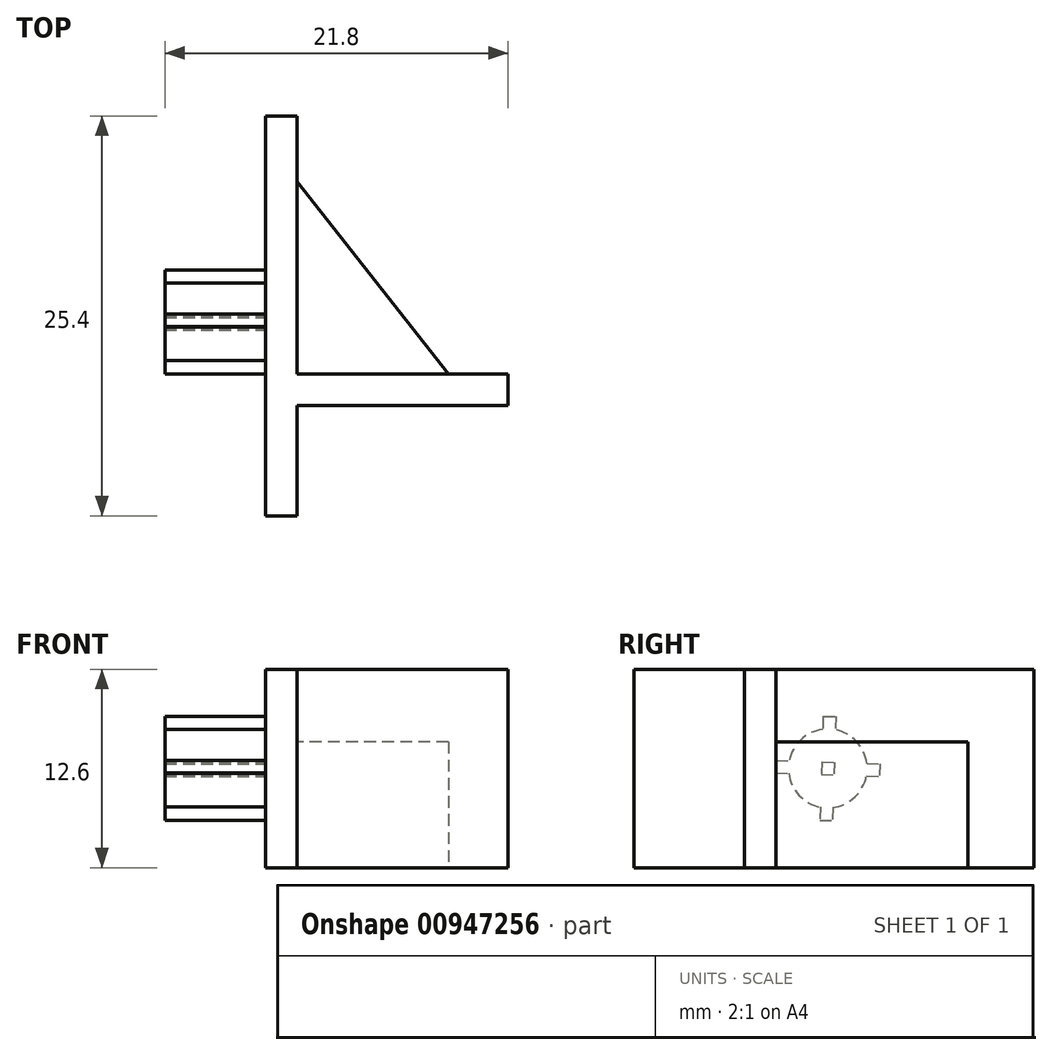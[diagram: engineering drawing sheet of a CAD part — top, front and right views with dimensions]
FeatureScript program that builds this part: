
annotation { "Feature Type Name" : "Feature", "Feature Type Description" : "" }
export const myFeature = defineFeature(function(context is Context, id is Id, definition is map)
    precondition{}
    {
        {
            var Q0;
            Q0=qCreatedBy(makeId("Top.planeOp"),FACE);
            var sketch = newSketch(context, id + "F0", { "sketchPlane" : qUnion([Q0])});
            skLineSegment(sketch, "E0", {"start": v(0, -10.12) * mm, "end": v(0, 15.28) * mm});
            skLineSegment(sketch, "E1", {"start": v(0, -10.12) * mm, "end": v(2, -10.12) * mm});
            skLineSegment(sketch, "E2", {"start": v(2, -10.12) * mm, "end": v(2, -3.12) * mm});
            skLineSegment(sketch, "E3", {"start": v(2, -3.12) * mm, "end": v(15.4, -3.12) * mm});
            skLineSegment(sketch, "E4", {"start": v(15.4, -3.12) * mm, "end": v(15.4, -1.12) * mm});
            skLineSegment(sketch, "E5", {"start": v(15.4, -1.12) * mm, "end": v(2, -1.12) * mm});
            skLineSegment(sketch, "E6", {"start": v(2, -1.12) * mm, "end": v(2, 15.28) * mm});
            skLineSegment(sketch, "E7", {"start": v(2, 15.28) * mm, "end": v(0, 15.28) * mm});
            skLineSegment(sketch, "E8", {"start": v(11.6, -1.12) * mm, "end": v(2, 11.1) * mm});
            skSolve(sketch);
        }
        {
            var Q0;
            {var subQ3=sQuery(id+"F0.wireOp",EDGE,"E8");Q0=makeQuery(id+"F0.imprint","IMPRINT",FACE,{"disambiguationData":[TD([[makeQuery(id+"F0.imprint","IMPRINT",EDGE,{"derivedFrom":subQ3}),1.0]])]});}
            extrude(context, id + "F1", {"entities" : qUnion([Q0]), "depth" : 8 * mm, "offsetDistance" : 25 * mm});
        }
        {
            var Q0;
            Q0=makeQuery(id+"F0.imprint","IMPRINT",FACE,{"disambiguationData":[TD([[makeQuery(id+"F0.imprint","IMPRINT",EDGE,{"derivedFrom":sQuery(id+"F0.wireOp",EDGE,"E0")}),-1.0]])]});
            extrude(context, id + "F2", {"entities" : qUnion([Q0]), "operationType" : NewBodyOperationType.ADD, "depth" : 12.6 * mm, "offsetDistance" : 25 * mm});
        }
        {
            var Q0;
            Q0=makeQuery(id+"F2.opExtrude","SWEPT_FACE",FACE,{"disambiguationData":[OSD([sQuery(id+"F0.wireOp",EDGE,"E0")])]});
            var sketch = newSketch(context, id + "F3", { "sketchPlane" : qUnion([Q0])});
            skCircle(sketch, "E9", {"center": v(-2.18, 6.3) * mm, "radius": 2.5 * mm});
            skLineSegment(sketch, "E10", {"start": v(-1.67, 3) * mm, "end": v(-2.47, 3) * mm});
            skLineSegment(sketch, "E11", {"start": v(-1.89, 9.6) * mm, "end": v(-2.69, 9.6) * mm});
            skPoint(sketch, "E12", {"position": v(-2.07, 3) * mm});
            skPoint(sketch, "E13", {"position": v(-2.29, 9.6) * mm});
            skLineSegment(sketch, "E14", {"start": v(-1.89, 9.6) * mm, "end": v(-1.67, 3) * mm});
            skLineSegment(sketch, "E15", {"start": v(-2.69, 9.6) * mm, "end": v(-2.47, 3) * mm});
            skLineSegment(sketch, "E16", {"start": v(1.1, 6.8) * mm, "end": v(1.13, 6) * mm});
            skLineSegment(sketch, "E17", {"start": v(-5.5, 6.6) * mm, "end": v(-5.47, 5.8) * mm});
            skPoint(sketch, "E18", {"position": v(-5.48, 6.2) * mm});
            skPoint(sketch, "E19", {"position": v(1.12, 6.4) * mm});
            skLineSegment(sketch, "E20", {"start": v(1.1, 6.8) * mm, "end": v(-5.5, 6.6) * mm});
            skLineSegment(sketch, "E21", {"start": v(1.13, 6) * mm, "end": v(-5.47, 5.8) * mm});
            skSolve(sketch);
        }
        {
            var Q0;
            Q0 = qSketchRegion(id + "F3", true);
            extrude(context, id + "F4", {"entities" : qUnion([Q0]), "operationType" : NewBodyOperationType.ADD, "depth" : 6.4 * mm, "offsetDistance" : 25 * mm});
        }
    });
